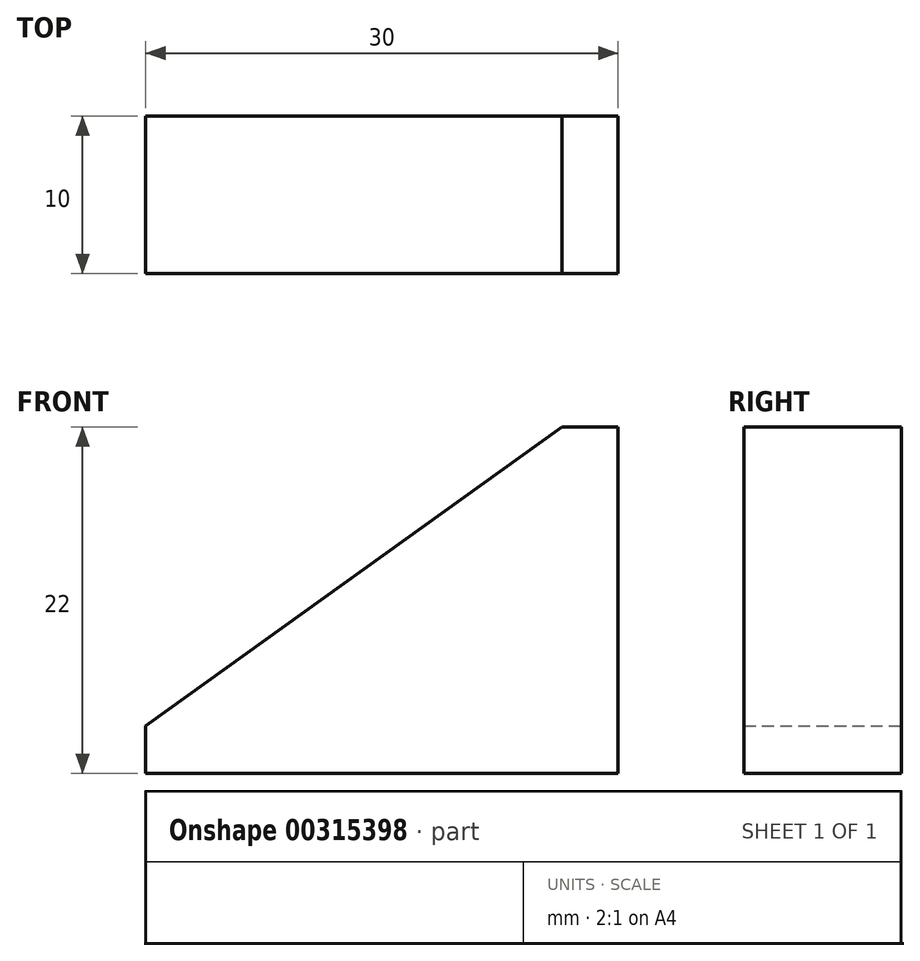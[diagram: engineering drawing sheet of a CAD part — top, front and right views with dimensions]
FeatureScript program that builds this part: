
annotation { "Feature Type Name" : "Feature", "Feature Type Description" : "" }
export const myFeature = defineFeature(function(context is Context, id is Id, definition is map)
    precondition{}
    {
        {
            var Q0;
            Q0=qCreatedBy(makeId("Front.planeOp"),FACE);
            var sketch = newSketch(context, id + "F0", { "sketchPlane" : qUnion([Q0])});
            skLineSegment(sketch, "E0", {"start": v(0, 0) * mm, "end": v(-34.2, 0) * mm});
            skLineSegment(sketch, "E1", {"start": v(-34.2, 0) * mm, "end": v(0, 24.56) * mm});
            skLineSegment(sketch, "E2", {"start": v(0, 24.56) * mm, "end": v(0, 0) * mm});
            skLineSegment(sketch, "E3", {"start": v(-30, 0) * mm, "end": v(-30, 3.02) * mm});
            skLineSegment(sketch, "E4", {"start": v(-3.56, 22) * mm, "end": v(0, 22) * mm});
            skSolve(sketch);
        }
        {
            var Q0;
            {var subQ0=sQuery(id+"F0.wireOp",EDGE,"E3");Q0=makeQuery(id+"F0.imprint","IMPRINT",FACE,{"disambiguationData":[TD([[makeQuery(id+"F0.imprint","IMPRINT",EDGE,{"derivedFrom":subQ0}),-1.0]])]});}
            extrude(context, id + "F1", {"entities" : qUnion([Q0]), "depth" : 10 * mm});
        }
    });
